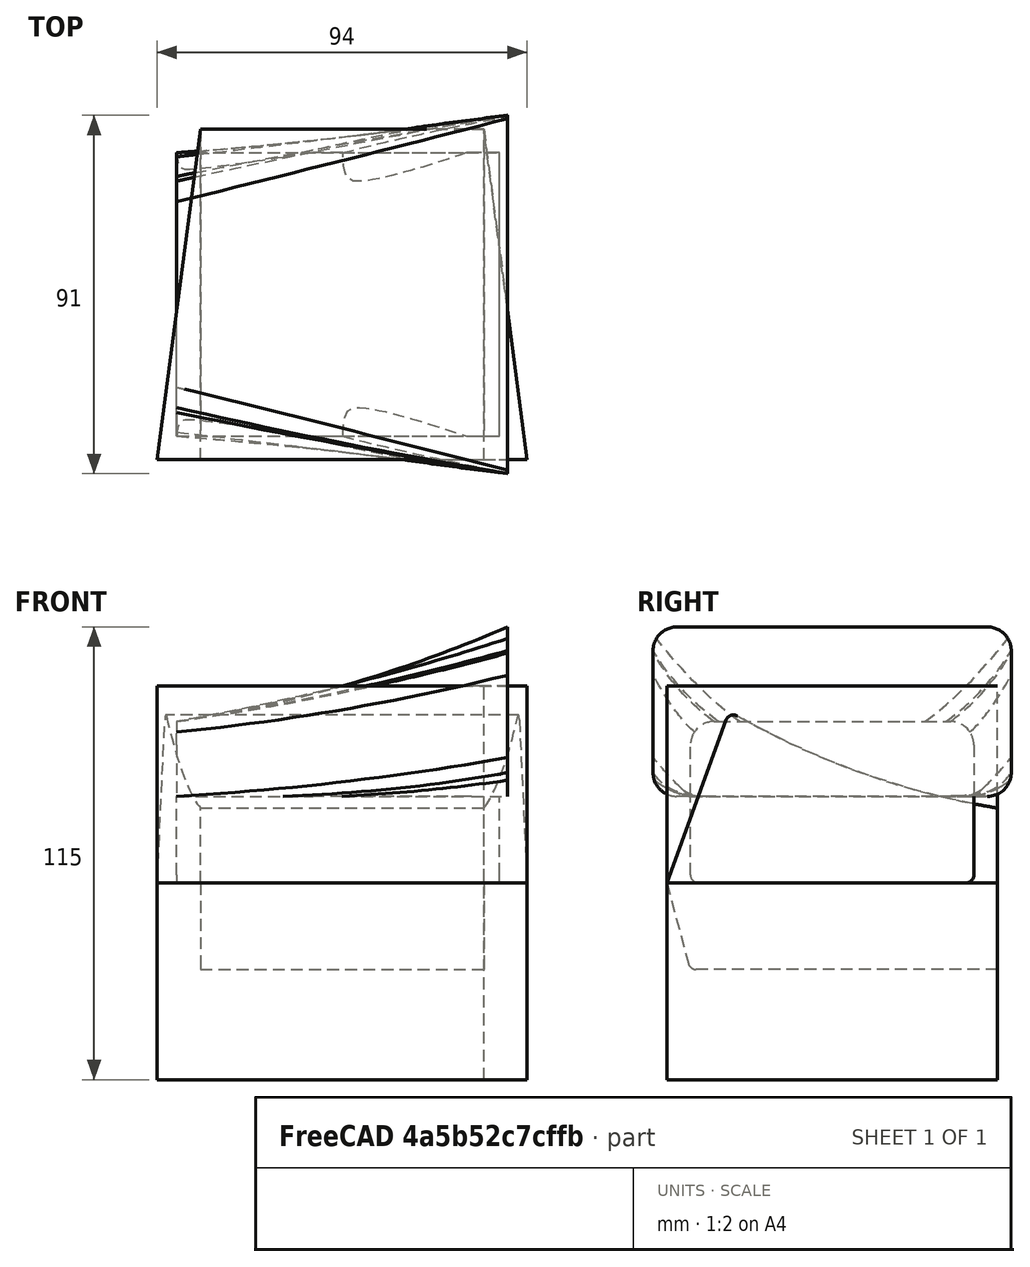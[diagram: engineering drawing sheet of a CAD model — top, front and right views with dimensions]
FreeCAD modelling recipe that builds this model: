
FCSTD DOCUMENT  (FreeCAD 0.19R24212 (Git))
Label: solder_station
License: All rights reserved
LicenseURL: http://en.wikipedia.org/wiki/All_rights_reserved
objects: Sketcher::SketchObject×11, PartDesign::Pad×4, PartDesign::Body×3, Spreadsheet::Sheet×1, Mesh::Feature×1, PartDesign::AdditiveLoft×1, PartDesign::Boolean×1, App::Part×1
note: 25 computed .brp shape members not serialized (recipe doc carries the construction recipe); baked Part::Feature solids carry a one-line shape summary decoded from their .brp

FEATURE [Sketcher::SketchObject] Sketch  label="RearSupport"
  AttachmentOffset = pos=(0,0,-42) rot=(0,0,1;0rad)
  FullyConstrained = true
  MapMode = 5
  Placement = pos=(-42,9.3e-15,-9.3e-15) rot=(0.57735,0.57735,0.57735;2.0944rad)
  Support = -> [YZ_Plane001]
  expr: Constraints[44] = 3
  expr: Constraints[16] = <<param>>.rear_width
  expr: Constraints[52] = <<param>>.wall * 2
  expr: Constraints[56] = <<param>>.wall * 2
  expr: Constraints[15] = Spreadsheet.radius_big
  expr: .AttachmentOffset.Base.z = -Spreadsheet.mid_depth / 2
  expr: Constraints[18] = <<param>>.rear_height
  expr: Constraints[17] = <<param>>.rear_width / 2
  expr: Constraints[55] = <<param>>.wall * 2
  expr: Constraints[53] = <<param>>.wall * 2
  expr: Constraints[54] = <<param>>.wall * 2
  expr: Constraints[57] = <<param>>.wall * 2
  sketch-geometry (24):
    g0: LineSegment StartX=-30 StartY=41 StartZ=0 EndX=30 EndY=41 EndZ=0
    g1: LineSegment StartX=36 StartY=35 StartZ=0 EndX=36 EndY=6 EndZ=0
    g2: LineSegment StartX=30 StartY=0 StartZ=0 EndX=-30 EndY=0 EndZ=0
    g3: LineSegment StartX=-36 StartY=6 StartZ=0 EndX=-36 EndY=35 EndZ=0
    g4: ArcOfCircle CenterX=-30 CenterY=35 CenterZ=0 NormalX=0 NormalY=0 NormalZ=1 AngleXU=0 Radius=6 StartAngle=1.5708 EndAngle=3.14159
    g5: ArcOfCircle CenterX=30 CenterY=35 CenterZ=0 NormalX=0 NormalY=0 NormalZ=1 AngleXU=0 Radius=6 StartAngle=-9e-16 EndAngle=1.5708
    g6: ArcOfCircle CenterX=30 CenterY=6 CenterZ=0 NormalX=0 NormalY=0 NormalZ=1 AngleXU=0 Radius=6 StartAngle=4.71239 EndAngle=6.28319
    g7: ArcOfCircle CenterX=-30 CenterY=6 CenterZ=0 NormalX=0 NormalY=0 NormalZ=1 AngleXU=0 Radius=6 StartAngle=3.14159 EndAngle=4.71239
    g8: LineSegment StartX=-26.6 StartY=34.6 StartZ=0 EndX=-9.4 EndY=34.6 EndZ=0
    g9: LineSegment StartX=29.6 StartY=31.6 StartZ=0 EndX=29.6 EndY=9.4 EndZ=0
    g10: LineSegment StartX=26.6 StartY=6.4 StartZ=0 EndX=9.4 EndY=6.4 EndZ=0
    g11: LineSegment StartX=-29.6 StartY=9.4 StartZ=0 EndX=-29.6 EndY=31.6 EndZ=0
    g12: LineSegment StartX=-6.4 StartY=31.6 StartZ=0 EndX=-6.4 EndY=9.4 EndZ=0
    g13: LineSegment StartX=6.4 StartY=31.6 StartZ=0 EndX=6.4 EndY=9.4 EndZ=0
    g14: LineSegment StartX=9.4 StartY=34.6 StartZ=0 EndX=26.6 EndY=34.6 EndZ=0
    g15: LineSegment StartX=-9.4 StartY=6.4 StartZ=0 EndX=-26.6 EndY=6.4 EndZ=0
    g16: ArcOfCircle CenterX=-9.4 CenterY=31.6 CenterZ=0 NormalX=0 NormalY=0 NormalZ=1 AngleXU=0 Radius=3 StartAngle=4e-16 EndAngle=1.5708
    g17: ArcOfCircle CenterX=9.4 CenterY=31.6 CenterZ=0 NormalX=0 NormalY=0 NormalZ=1 AngleXU=0 Radius=3 StartAngle=1.5708 EndAngle=3.14159
    g18: ArcOfCircle CenterX=-9.4 CenterY=9.4 CenterZ=0 NormalX=0 NormalY=0 NormalZ=1 AngleXU=0 Radius=3 StartAngle=4.71239 EndAngle=6.28319
    g19: ArcOfCircle CenterX=9.4 CenterY=9.4 CenterZ=0 NormalX=0 NormalY=0 NormalZ=1 AngleXU=0 Radius=3 StartAngle=3.14159 EndAngle=4.71239
    g20: ArcOfCircle CenterX=-26.6 CenterY=31.6 CenterZ=0 NormalX=0 NormalY=0 NormalZ=1 AngleXU=0 Radius=3 StartAngle=1.5708 EndAngle=3.14159
    g21: ArcOfCircle CenterX=-26.6 CenterY=9.4 CenterZ=0 NormalX=0 NormalY=0 NormalZ=1 AngleXU=0 Radius=3 StartAngle=3.14159 EndAngle=4.71239
    g22: ArcOfCircle CenterX=26.6 CenterY=31.6 CenterZ=0 NormalX=0 NormalY=0 NormalZ=1 AngleXU=0 Radius=3 StartAngle=2e-16 EndAngle=1.5708
    g23: ArcOfCircle CenterX=26.6 CenterY=9.4 CenterZ=0 NormalX=0 NormalY=0 NormalZ=1 AngleXU=0 Radius=3 StartAngle=4.71239 EndAngle=6.28319
  constraints (58):
    c: Horizontal(g0)
    c: Horizontal(g2)
    c: Vertical(g1)
    c: Vertical(g3)
    c: Tangent(g3,g4) = 1.5708
    c: Tangent(g0,g4) = 1.5708
    c: Tangent(g0,g5) = 1.5708
    c: Tangent(g1,g5) = 1.5708
    c: Tangent(g1,g6) = 1.5708
    c: Tangent(g2,g6) = 1.5708
    c: Tangent(g2,g7) = 1.5708
    c: Tangent(g3,g7) = 1.5708
    c: Equal(g4,g7)
    c: Equal(g7,g6)
    c: Equal(g6,g5)
    c: Radius(g4) = 6
    c: DistanceX(g3,g1) = 72
    c: DistanceX(g3,g-1) = 36
    c: DistanceY(g2,g0) = 41
    c: Horizontal(g8)
    c: Horizontal(g10)
    c: Vertical(g9)
    c: Vertical(g11)
    c: Vertical(g12)
    c: Vertical(g13)
    c: PointOnObject(g-1,g2)
    c: Tangent(g8,g14)
    c: Tangent(g10,g15)
    c: Tangent(g8,g16) = 1.5708
    c: Tangent(g12,g16) = 1.5708
    c: Tangent(g13,g17) = -1.5708
    c: Tangent(g14,g17) = 1.5708
    c: Tangent(g15,g18) = 1.5708
    c: Tangent(g12,g18) = 1.5708
    c: Tangent(g13,g19) = -1.5708
    c: Tangent(g10,g19) = 1.5708
    c: Tangent(g8,g20) = 1.5708
    c: Tangent(g11,g20) = 1.5708
    c: Tangent(g11,g21) = 1.5708
    c: Tangent(g15,g21) = 1.5708
    c: Tangent(g14,g22) = 1.5708
    c: Tangent(g9,g22) = 1.5708
    c: Tangent(g9,g23) = 1.5708
    c: Tangent(g10,g23) = 1.5708
    c: Radius(g17) = 3
    c: Equal(g20,g21)
    c: Equal(g21,g18)
    c: Equal(g18,g16)
    c: Equal(g16,g19)
    c: Equal(g19,g23)
    c: Equal(g23,g22)
    c: Equal(g22,g17)
    c: DistanceY(g-1,g15) = 6.4
    c: DistanceX(g3,g11) = 6.4
    c: DistanceX(g9,g1) = 6.4
    c: DistanceX(g12,g-1) = 6.4
    c: DistanceX(g-1,g13) = 6.4
    c: DistanceY(g14,g0) = 6.4
FEATURE [Sketcher::SketchObject] Sketch001  label="Front"
  AttachmentOffset = pos=(0,0,42) rot=(1,0,0;0rad)
  FullyConstrained = true
  MapMode = 5
  Placement = pos=(42,-9.3e-15,9.3e-15) rot=(0.57735,0.57735,0.57735;2.0944rad)
  Support = -> [YZ_Plane001]
  expr: .AttachmentOffset.Base.z = Spreadsheet.mid_depth / 2
  expr: Constraints[3] = Spreadsheet.radius_big
  expr: Constraints[4] = Spreadsheet.front_width1
  expr: Constraints[18] = <<param>>.front_height
  expr: Constraints[23] = <<param>>.bottom_height
  sketch-geometry (8):
    g0: LineSegment StartX=-39.5 StartY=65 StartZ=0 EndX=39.5 EndY=65 EndZ=0
    g1: ArcOfCircle CenterX=-39.5 CenterY=59 CenterZ=0 NormalX=0 NormalY=0 NormalZ=1 AngleXU=0 Radius=6 StartAngle=1.5708 EndAngle=3.14159
    g2: ArcOfCircle CenterX=39.5 CenterY=59 CenterZ=0 NormalX=0 NormalY=0 NormalZ=1 AngleXU=0 Radius=6 StartAngle=0 EndAngle=1.5708
    g3: LineSegment StartX=-45.5 StartY=59 StartZ=0 EndX=-45.5 EndY=28 EndZ=0
    g4: LineSegment StartX=45.5 StartY=59 StartZ=0 EndX=45.5 EndY=28 EndZ=0
    g5: ArcOfCircle CenterX=39.5 CenterY=28 CenterZ=0 NormalX=0 NormalY=0 NormalZ=1 AngleXU=0 Radius=6 StartAngle=4.71239 EndAngle=6.28319
    g6: ArcOfCircle CenterX=-39.5 CenterY=28 CenterZ=0 NormalX=0 NormalY=0 NormalZ=1 AngleXU=0 Radius=6 StartAngle=3.14159 EndAngle=4.71239
    g7: LineSegment StartX=-39.5 StartY=22 StartZ=0 EndX=39.5 EndY=22 EndZ=0
  constraints (25):
    c: Horizontal(g0)
    c: Tangent(g0,g1) = 1.5708
    c: Tangent(g0,g2) = 1.5708
    c: Radius(g1) = 6
    c: DistanceX(g1,g2) = 91
    c: Horizontal(g2,g2)
    c: Horizontal(g1,g1)
    c: Coincident(g3,g1)
    c: Vertical(g3)
    c: Coincident(g4,g2)
    c: Vertical(g4)
    c: Coincident(g5,g4)
    c: Horizontal(g5,g4)
    c: Equal(g1,g2)
    c: Equal(g3,g4)
    c: Coincident(g6,g3)
    c: Horizontal(g3,g6)
    c: Vertical(g6,g6)
    c: DistanceY(g-1,g0) = 65
    c: Vertical(g5,g5)
    c: Coincident(g7,g6)
    c: Coincident(g7,g5)
    c: Symmetric(g6,g5,g-2)
    c: DistanceY(g-1,g5) = 22
    c: Equal(g5,g2)
FEATURE [Sketcher::SketchObject] Sketch003  label="Mid"
  FullyConstrained = true
  MapMode = 5
  Placement = pos=(0,0,0) rot=(0.57735,0.57735,0.57735;2.0944rad)
  Support = -> [YZ_Plane001]
  expr: Constraints[2] = Spreadsheet.radius_big
  expr: Constraints[19] = <<param>>.bottom_height
  expr: Constraints[15] = Spreadsheet.center_width
  expr: Constraints[20] = Spreadsheet.center_height
  expr: Constraints[22] = <<param>>.bottom_width
  sketch-geometry (8):
    g0: LineSegment StartX=-34 StartY=50 StartZ=0 EndX=34 EndY=50 EndZ=0
    g1: ArcOfCircle CenterX=-34 CenterY=44 CenterZ=0 NormalX=0 NormalY=0 NormalZ=1 AngleXU=0 Radius=6 StartAngle=1.5708 EndAngle=3.14159
    g2: ArcOfCircle CenterX=34 CenterY=44 CenterZ=0 NormalX=0 NormalY=0 NormalZ=1 AngleXU=0 Radius=6 StartAngle=-1.8e-15 EndAngle=1.5708
    g3: LineSegment StartX=-40 StartY=44 StartZ=0 EndX=-40 EndY=26 EndZ=0
    g4: LineSegment StartX=40 StartY=44 StartZ=0 EndX=40 EndY=26 EndZ=0
    g5: ArcOfCircle CenterX=-36 CenterY=26 CenterZ=0 NormalX=0 NormalY=0 NormalZ=1 AngleXU=0 Radius=4 StartAngle=3.14159 EndAngle=4.71239
    g6: ArcOfCircle CenterX=36 CenterY=26 CenterZ=0 NormalX=0 NormalY=0 NormalZ=1 AngleXU=0 Radius=4 StartAngle=4.71239 EndAngle=6.28319
    g7: LineSegment StartX=-36 StartY=22 StartZ=0 EndX=36 EndY=22 EndZ=0
  constraints (24):
    c: Tangent(g0,g1) = 1.5708
    c: Tangent(g0,g2) = 1.5708
    c: Radius(g1) = 6
    c: Equal(g1,g2)
    c: Horizontal(g1,g1)
    c: Coincident(g3,g1)
    c: Coincident(g4,g2)
    c: Vertical(g4)
    c: Vertical(g3)
    c: Equal(g4,g3)
    c: Coincident(g5,g3)
    c: Coincident(g6,g4)
    c: Horizontal(g3,g5)
    c: Horizontal(g6,g4)
    c: Symmetric(g0,g0,g-2)
    c: DistanceX(g1,g2) = 80
    c: Vertical(g6,g6)
    c: Coincident(g7,g5)
    c: Coincident(g7,g6)
    c: DistanceY(g-1,g6) = 22
    c: DistanceY(g-1,g0) = 50
    c: Vertical(g5,g5)
    c: DistanceX(g5,g6) = 72
    c: Symmetric(g5,g6,g-2)
FEATURE [Spreadsheet::Sheet] Spreadsheet  label="param"
  cells = A1=Body; B2=top_depth; C2(top_depth)=70; B3=mid_depth; C3(mid_depth)=84; B4=bottom_depth; C4(bottom_depth)=75; B6=bottom_width; C6(bottom_width)=72; B7=bottom_height; C7(bottom_height)=22; B8=bottom_angle; C8(bottom_angle)=15; B10=rear_width; C10(rear_width)=72; B11=rear_height; C11(rear_height)=41; B13=center_width; C13(center_width)=80; B14=center_height; C14(center_height)=50; B16=front_width1; C16(front_width1)=91; D16=@top; E16=not used; B17=front_width2; C17(front_width2)=94; D17=@mid; B18=front_height; C18(front_height)=65; B19=front_wall; C19(front_wall)=5; B20=front_face; C20(front_face)=44; B21=front_angle; C21(front_angle)=20; B23=wall; C23(wall)=3.2; B24=radius_big; C24(radius_big)=6; B25=radius_small; C25(radius_small)=2; B26=arch; C26(arch)=200; A28=Box Interior; B30=hole_inside; C30(hole_inside)=16; B31=hole_outside; C31(hole_outside)=20; B32=hole_height; C32(hole_height)=7; B33=hole_angle; C33(hole_angle)=-20; A35=Battery Cuts
FEATURE [Sketcher::SketchObject] Sketch007  label="Button"
  AttachmentOffset = pos=(0,0,49) rot=(0,1,0;-0.349066rad)
  FullyConstrained = true
  MapMode = 5
  Placement = pos=(0,0,49) rot=(0,1,0;5.93412rad)
  Support = -> [XY_Plane001]
  expr: .AttachmentOffset.Rotation.Angle = <<param>>.hole_angle
  expr: Constraints[1] = <<param>>.hole_outside
  expr: .AttachmentOffset.Base.z = Spreadsheet.center_height - 1
  sketch-geometry (1):
    g0: Circle CenterX=0 CenterY=0 CenterZ=0 NormalX=0 NormalY=0 NormalZ=1 AngleXU=0 Radius=10
  constraints (2):
    c: Coincident(g0,g-1)
    c: Diameter(g0) = 20
FEATURE [Sketcher::SketchObject] Sketch008  label="Upper Button"
  AttachmentOffset = pos=(0,0,50) rot=(0,1,0;-0.349066rad)
  FullyConstrained = true
  MapMode = 5
  Placement = pos=(0,0,50) rot=(0,1,0;5.93412rad)
  Support = -> [XY_Plane001]
  expr: .AttachmentOffset.Base.z = Spreadsheet.center_height
  expr: Constraints[1] = <<param>>.hole_inside
  expr: .AttachmentOffset.Rotation.Angle = <<param>>.hole_angle
  sketch-geometry (1):
    g0: Circle CenterX=0 CenterY=0 CenterZ=0 NormalX=0 NormalY=0 NormalZ=1 AngleXU=0 Radius=8
  constraints (2):
    c: Coincident(g0,g-1)
    c: Diameter(g0) = 16
FEATURE [Sketcher::SketchObject] Sketch009  label="Rear"
  AttachmentOffset = pos=(0,0,-42) rot=(0,0,1;0rad)
  FullyConstrained = true
  MapMode = 5
  Placement = pos=(-42,9.3e-15,-9.3e-15) rot=(0.57735,0.57735,0.57735;2.0944rad)
  Support = -> [YZ_Plane001]
  expr: Constraints[2] = <<param>>.rear_width / 2
  expr: .AttachmentOffset.Base.z = -Spreadsheet.mid_depth / 2
  expr: Constraints[12] = <<param>>.radius_big
  expr: Constraints[6] = <<param>>.rear_width
  expr: Constraints[16] = <<param>>.bottom_height
  expr: Constraints[17] = <<param>>.rear_height
  sketch-geometry (6):
    g0: LineSegment StartX=-30 StartY=41 StartZ=0 EndX=30 EndY=41 EndZ=0
    g1: ArcOfCircle CenterX=-30 CenterY=35 CenterZ=0 NormalX=0 NormalY=0 NormalZ=1 AngleXU=0 Radius=6 StartAngle=1.5708 EndAngle=3.14159
    g2: ArcOfCircle CenterX=30 CenterY=35 CenterZ=0 NormalX=0 NormalY=0 NormalZ=1 AngleXU=0 Radius=6 StartAngle=0 EndAngle=1.5708
    g3: LineSegment StartX=36 StartY=35 StartZ=0 EndX=36 EndY=22 EndZ=0
    g4: LineSegment StartX=-36 StartY=35 StartZ=0 EndX=-36 EndY=22 EndZ=0
    g5: LineSegment StartX=-36 StartY=22 StartZ=0 EndX=36 EndY=22 EndZ=0
  constraints (20):
    c: Horizontal(g0)
    c: Coincident(g1,g0)
    c: DistanceX(g4,g-1) = 36
    c: Coincident(g0,g2)
    c: Tangent(g2,g0)
    c: Tangent(g1,g0)
    c: DistanceX(g4,g3) = 72
    c: Coincident(g3,g2)
    c: Vertical(g3)
    c: Coincident(g4,g1)
    c: Vertical(g4)
    c: Equal(g1,g2)
    c: Radius(g1) = 6
    c: Equal(g3,g4)
    c: Horizontal(g2,g2)
    c: Horizontal(g5)
    c: DistanceY(g-1,g5) = 22
    c: DistanceY(g-1,g0) = 41
    c: Coincident(g5,g3)
    c: Coincident(g4,g5)
FEATURE [Mesh::Feature] M18_soldering_case
  Placement = pos=(48,-41,-22) rot=(0,0.707107,0.707107;3.14159rad)
FEATURE [Sketcher::SketchObject] Sketch010  label="BottomRear"
  AttachmentOffset = pos=(0,0.01,-42) rot=(0,0,1;0rad)
  FullyConstrained = true
  MapMode = 5
  Placement = pos=(-42,9.3e-15,0.01) rot=(0.57735,0.57735,0.57735;2.0944rad)
  Support = -> [YZ_Plane001]
  expr: .AttachmentOffset.Base.z = -Spreadsheet.mid_depth / 2
  expr: Constraints[13] = <<param>>.radius_small
  expr: Constraints[17] = <<param>>.bottom_height
  expr: Constraints[18] = <<param>>.bottom_width
  sketch-geometry (6):
    g0: LineSegment StartX=-34 StartY=0 StartZ=0 EndX=34 EndY=-1.3e-15 EndZ=0
    g1: LineSegment StartX=36 StartY=2 StartZ=0 EndX=36 EndY=22 EndZ=0
    g2: LineSegment StartX=-36 StartY=2 StartZ=0 EndX=-36 EndY=22 EndZ=0
    g3: LineSegment StartX=-36 StartY=22 StartZ=0 EndX=36 EndY=22 EndZ=0
    g4: ArcOfCircle CenterX=34 CenterY=2 CenterZ=0 NormalX=0 NormalY=0 NormalZ=1 AngleXU=0 Radius=2 StartAngle=4.71239 EndAngle=6.28319
    g5: ArcOfCircle CenterX=-34 CenterY=2 CenterZ=0 NormalX=0 NormalY=0 NormalZ=1 AngleXU=0 Radius=2 StartAngle=3.14159 EndAngle=4.71239
  constraints (19):
    c: PointOnObject(g0,g-1)
    c: PointOnObject(g0,g-1)
    c: Vertical(g1)
    c: Vertical(g2)
    c: Coincident(g3,g1)
    c: Coincident(g3,g2)
    c: Coincident(g4,g1)
    c: Coincident(g4,g0)
    c: Coincident(g5,g2)
    c: Coincident(g5,g0)
    c: Equal(g1,g2)
    c: Symmetric(g2,g1,g-2)
    c: Equal(g4,g5)
    c: Radius(g5) = 2
    c: Vertical(g0,g4)
    c: Horizontal(g4,g1)
    c: Vertical(g0,g5)
    c: DistanceY(g-1,g1) = 22
    c: DistanceX(g2,g1) = 72
FEATURE [PartDesign::AdditiveLoft] AdditiveLoft
  Closed = false
  Placement = pos=(0,0,0) rot=(0.57735,0.57735,0.57735;2.0944rad)
  Profile = -> Sketch009
  Ruled = false
  Sections = -> [Sketch003,Sketch001]
FEATURE [Sketcher::SketchObject] Sketch011  label="BottomFront"
  AttachmentOffset = pos=(0,0,42) rot=(1,0,0;0rad)
  FullyConstrained = true
  MapMode = 5
  Placement = pos=(42,-9.3e-15,9.3e-15) rot=(0.57735,0.57735,0.57735;2.0944rad)
  Support = -> [YZ_Plane001]
  expr: .AttachmentOffset.Rotation.Angle = 0
  expr: .AttachmentOffset.Base.z = Spreadsheet.mid_depth / 2
  expr: Constraints[11] = <<param>>.bottom_height
  expr: Constraints[10] = <<param>>.bottom_width
  expr: Constraints[9] = <<param>>.radius_small
  sketch-geometry (6):
    g0: LineSegment StartX=-34 StartY=4e-16 StartZ=0 EndX=34 EndY=-1.8e-15 EndZ=0
    g1: LineSegment StartX=36 StartY=2 StartZ=0 EndX=36 EndY=22 EndZ=0
    g2: ArcOfCircle CenterX=34 CenterY=2 CenterZ=0 NormalX=0 NormalY=0 NormalZ=1 AngleXU=0 Radius=2 StartAngle=4.71239 EndAngle=6.28319
    g3: ArcOfCircle CenterX=-34 CenterY=2 CenterZ=0 NormalX=0 NormalY=0 NormalZ=1 AngleXU=0 Radius=2 StartAngle=3.14159 EndAngle=4.71239
    g4: LineSegment StartX=-36 StartY=22 StartZ=0 EndX=-36 EndY=2 EndZ=0
    g5: LineSegment StartX=-36 StartY=22 StartZ=0 EndX=36 EndY=22 EndZ=0
  constraints (19):
    c: PointOnObject(g0,g-1)
    c: Vertical(g1)
    c: Coincident(g2,g1)
    c: Coincident(g2,g0)
    c: Coincident(g3,g0)
    c: Coincident(g4,g3)
    c: Vertical(g4)
    c: Symmetric(g0,g0,g-2)
    c: Equal(g3,g2)
    c: Radius(g2) = 2
    c: DistanceX(g3,g1) = 72
    c: DistanceY(g-1,g1) = 22
    c: Horizontal(g3,g3)
    c: Vertical(g0,g3)
    c: Horizontal(g2,g1)
    c: Vertical(g2,g0)
    c: Equal(g1,g4)
    c: Coincident(g5,g4)
    c: Coincident(g5,g1)
FEATURE [Sketcher::SketchObject] Sketch012  label="SketchSide"
  FullyConstrained = true
  MapMode = 5
  Placement = pos=(0,0,0) rot=(0.57735,0.57735,0.57735;2.0944rad)
  Support = -> [YZ_Plane002]
  expr: Constraints[8] = <<param>>.rear_height - <<param>>.bottom_height
  expr: Constraints[9] = <<param>>.radius_small
  expr: Constraints[14] = <<param>>.front_face
  expr: Constraints[10] = <<param>>.arch
  expr: Constraints[11] = 90 - <<param>>.front_angle
  expr: Constraints[12] = <<param>>.mid_depth
  sketch-geometry (5):
    g0: LineSegment StartX=-42 StartY=0 StartZ=0 EndX=42 EndY=0 EndZ=0
    g1: LineSegment StartX=42 StartY=0 StartZ=0 EndX=42 EndY=19 EndZ=0
    g2: LineSegment StartX=-42 StartY=0 StartZ=0 EndX=-26.9511 EndY=41.3465 EndZ=0
    g3: ArcOfCircle CenterX=-25.0717 CenterY=40.6624 CenterZ=0 NormalX=0 NormalY=0 NormalZ=1 AngleXU=0 Radius=2 StartAngle=1.05429 EndAngle=2.79253
    g4: ArcOfCircle CenterX=74.6859 CenterY=216.311 CenterZ=0 NormalX=0 NormalY=0 NormalZ=1 AngleXU=0 Radius=200 StartAngle=4.19588 EndAngle=4.54822
  constraints (15):
    c: PointOnObject(g0,g-1)
    c: Coincident(g1,g0)
    c: Vertical(g1)
    c: Coincident(g2,g0)
    c: Coincident(g3,g2)
    c: Coincident(g4,g1)
    c: Tangent(g4,g3) = 1.5708
    c: Symmetric(g0,g0,g-2)
    c: DistanceY(g1,g1) = 19
    c: Radius(g3) = 2
    c: Radius(g4) = 200
    c: Angle(g0,g2) = 1.22173
    c: DistanceX(g0,g0) = 84
    c: Tangent(g3,g2)
    c: Distance(g2) = 44
FEATURE [PartDesign::Pad] Pad  label="PadSide"
  Direction = (1,1,1)
  Length = 120
  Length2 = 100
  Midplane = true
  Placement = pos=(0,0,0) rot=(0.57735,0.57735,0.57735;2.0944rad)
  Profile = -> Sketch012
  Type = 0
FEATURE [Sketcher::SketchObject] Sketch013  label="SketchTop"
  FullyConstrained = true
  MapMode = 5
  Support = -> [XY_Plane003]
  expr: Constraints[4] = <<param>>.front_width2
  expr: Constraints[6] = <<param>>.rear_width
  expr: Constraints[8] = <<param>>.mid_depth
  expr: Constraints[9] = <<param>>.mid_depth / 2
  sketch-geometry (4):
    g0: LineSegment StartX=36 StartY=42 StartZ=0 EndX=-36 EndY=42 EndZ=0
    g1: LineSegment StartX=-36 StartY=42 StartZ=0 EndX=-47 EndY=-42 EndZ=0
    g2: LineSegment StartX=-47 StartY=-42 StartZ=0 EndX=47 EndY=-42 EndZ=0
    g3: LineSegment StartX=47 StartY=-42 StartZ=0 EndX=36 EndY=42 EndZ=0
  constraints (10):
    c: Coincident(g0,g1)
    c: Coincident(g1,g2)
    c: Coincident(g2,g3)
    c: Coincident(g3,g0)
    c: DistanceX(g1,g2) = 94
    c: Symmetric(g2,g1,g-2)
    c: DistanceX(g0,g0) = 72
    c: Symmetric(g0,g0,g-2)
    c: DistanceY(g2,g0) = 84
    c: DistanceY(g2,g-1) = 42
FEATURE [PartDesign::Pad] Pad001  label="PadTop"
  Direction = (1,1,1)
  Length = 100
  Length2 = 100
  Midplane = true
  Profile = -> Sketch013
  Type = 0
FEATURE [PartDesign::Body] Body002  label="BodyTop"
  Group = -> [Sketch013,Pad001]
  Origin = -> Origin003
  Tip = -> Pad001
FEATURE [PartDesign::Pad] Pad002
  BaseFeature = -> AdditiveLoft
  Direction = (1,1,1)
  Length = 82
  Length2 = 100
  Placement = pos=(0,0,0) rot=(0.57735,0.57735,0.57735;2.0944rad)
  Profile = -> Sketch010
  Type = 0
FEATURE [PartDesign::Body] Body
  Group = -> [Sketch,Sketch001,Sketch003,Sketch007,Sketch008,Sketch009,Sketch010,AdditiveLoft,Sketch011,Pad002]
  Origin = -> Origin001
  Tip = -> Pad002
FEATURE [PartDesign::Boolean] Boolean
  BaseFeature = -> Pad
  Group = -> [Body002]
  Type = 2
FEATURE [Sketcher::SketchObject] Sketch016  label="SketchBottom"
  FullyConstrained = true
  MapMode = 5
  Placement = pos=(0,0,0) rot=(0.57735,0.57735,0.57735;2.0944rad)
  Support = -> [YZ_Plane002]
  expr: Constraints[7] = <<param>>.bottom_height
  expr: Constraints[8] = <<param>>.mid_depth
  expr: Constraints[9] = 90 - <<param>>.bottom_angle
  expr: Constraints[12] = <<param>>.radius_small
  sketch-geometry (5):
    g0: LineSegment StartX=-42 StartY=0 StartZ=0 EndX=42 EndY=0 EndZ=0
    g1: LineSegment StartX=42 StartY=0 StartZ=0 EndX=42 EndY=-22 EndZ=0
    g2: LineSegment StartX=42 StartY=-22 StartZ=0 EndX=-34.5705 EndY=-22 EndZ=0
    g3: LineSegment StartX=-42 StartY=0 StartZ=0 EndX=-36.5023 EndY=-20.5176 EndZ=0
    g4: ArcOfCircle CenterX=-34.5705 CenterY=-20 CenterZ=0 NormalX=0 NormalY=0 NormalZ=1 AngleXU=0 Radius=2 StartAngle=3.40339 EndAngle=4.71239
  constraints (13):
    c: PointOnObject(g0,g-1)
    c: Coincident(g1,g0)
    c: Vertical(g1)
    c: Coincident(g2,g1)
    c: Horizontal(g2)
    c: Coincident(g3,g0)
    c: Symmetric(g0,g0,g-2)
    c: DistanceY(g1,g1) = 22
    c: DistanceX(g0,g0) = 84
    c: Angle(g3,g0) = 1.309
    c: Tangent(g3,g4) = -1.5708
    c: Tangent(g2,g4) = 1.5708
    c: Radius(g4) = 2
FEATURE [PartDesign::Pad] Pad003
  BaseFeature = -> Boolean
  Direction = (1,1,1)
  Length = 72
  Length2 = 100
  Midplane = true
  Profile = -> Sketch016
  Type = 0
  expr: Length = <<param>>.bottom_width
FEATURE [PartDesign::Body] Body001  label="BodySide"
  Group = -> [Sketch012,Pad,Boolean,Sketch016,Pad003]
  Origin = -> Origin002
  Tip = -> Pad003
FEATURE [App::Part] Part
  Group = -> [Body,Body001]
  Origin = -> Origin
